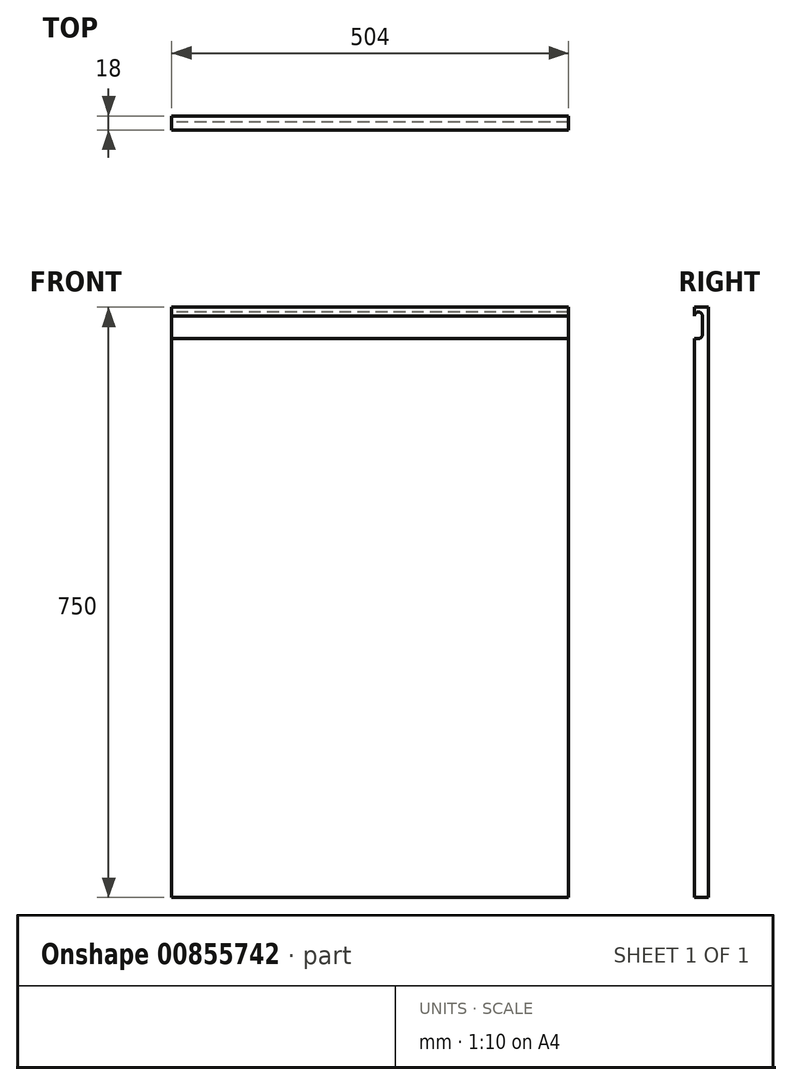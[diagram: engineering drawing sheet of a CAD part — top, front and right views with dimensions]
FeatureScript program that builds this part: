
annotation { "Feature Type Name" : "Feature", "Feature Type Description" : "" }
export const myFeature = defineFeature(function(context is Context, id is Id, definition is map)
    precondition{}
    {
        {
            var Q0;
            Q0=qCreatedBy(makeId("Front.planeOp"),FACE);
            var sketch = newSketch(context, id + "F0", { "sketchPlane" : qUnion([Q0])});
            skLineSegment(sketch, "E0", {"start": v(243.93, 383.36) * mm, "end": v(243.93, -366.64) * mm});
            skLineSegment(sketch, "E1", {"start": v(243.93, -366.64) * mm, "end": v(-8.07, -366.64) * mm});
            skLineSegment(sketch, "E2", {"start": v(-260.07, 383.36) * mm, "end": v(-260.07, -366.64) * mm});
            skLineSegment(sketch, "E3.trimOffspring", {"start": v(-260.07, 383.36) * mm, "end": v(-8.07, 383.36) * mm});
            skLineSegment(sketch, "E4", {"start": v(-8.07, -366.64) * mm, "end": v(-260.07, -366.64) * mm});
            skLineSegment(sketch, "E5", {"start": v(-8.07, 383.36) * mm, "end": v(243.93, 383.36) * mm});
            skSolve(sketch);
        }
        {
            var Q0;
            Q0=makeQuery(id+"F0.imprint","IMPRINT",FACE,{"disambiguationData":[TD([[makeQuery(id+"F0.imprint","IMPRINT",EDGE,{"derivedFrom":sQuery(id+"F0.wireOp",EDGE,"E0")}),-1.0]])]});
            extrude(context, id + "F1", {"entities" : qUnion([Q0]), "depth" : 18 * mm, "offsetDistance" : 25 * mm});
        }
        {
            var Q0;
            Q0=makeQuery(id+"F1.opExtrude","SWEPT_FACE",FACE,{"disambiguationData":[OSD([sQuery(id+"F0.wireOp",EDGE,"E2")])]});
            var sketch = newSketch(context, id + "F2", { "sketchPlane" : qUnion([Q0])});
            skLineSegment(sketch, "E6", {"start": v(18, 343.36) * mm, "end": v(13, 343.36) * mm});
            skLineSegment(sketch, "E7", {"start": v(8, 348.36) * mm, "end": v(8, 372.36) * mm});
            skArc(sketch, "E8", {"start": v(18, 372.36) * mm, "mid": v(13, 377.36) * mm, "end": v(8, 372.36) * mm});
            skPoint(sketch, "E9.visualSharp", {"position": v(8, 343.36) * mm});
            skArc(sketch, "E9.filletArc", {"start": v(8, 348.36) * mm, "mid": v(9.46, 344.82) * mm, "end": v(13, 343.36) * mm});
            skSolve(sketch);
        }
        {
            var Q0;
            {var subQ1=sQuery(id+"F2.wireOp",EDGE,"E6");Q0=makeQuery(id+"F2.imprint","IMPRINT",FACE,{"disambiguationData":[TD([[makeQuery(id+"F2.imprint","IMPRINT",EDGE,{"derivedFrom":subQ1}),-1.0]])]});}
            extrude(context, id + "F3", {"entities" : qUnion([Q0]), "operationType" : NewBodyOperationType.REMOVE, "oppositeDirection" : true, "depth" : 555 * mm, "offsetDistance" : 25 * mm});
        }
    });
